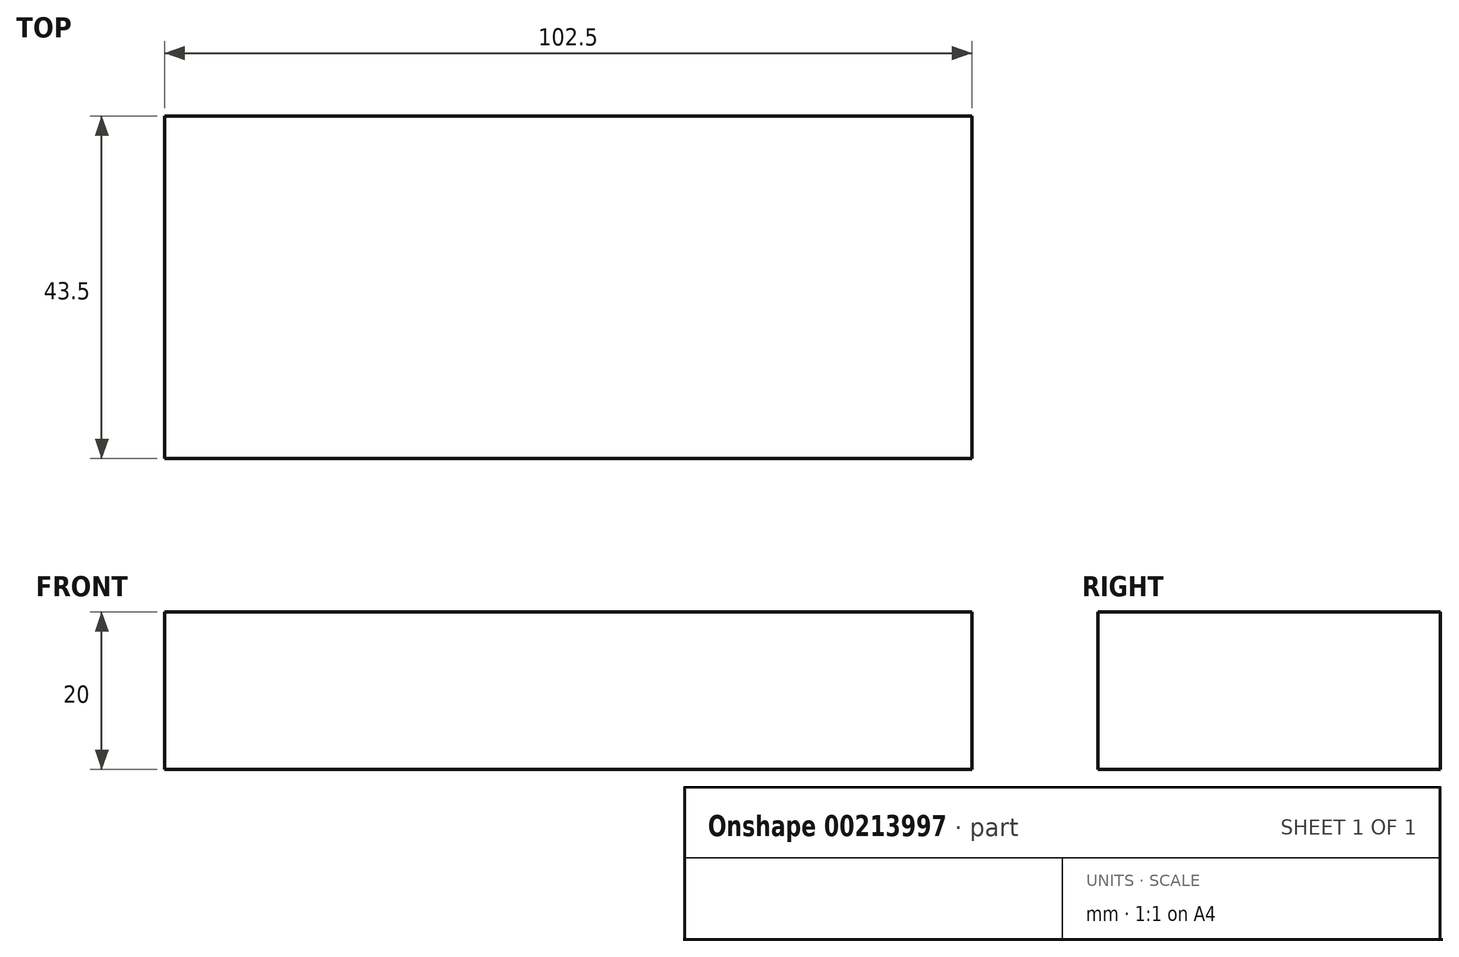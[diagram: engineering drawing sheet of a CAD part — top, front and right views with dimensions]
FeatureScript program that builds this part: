
annotation { "Feature Type Name" : "Feature", "Feature Type Description" : "" }
export const myFeature = defineFeature(function(context is Context, id is Id, definition is map)
    precondition{}
    {
        {
            var Q0;
            Q0=qCreatedBy(makeId("Top.planeOp"),FACE);
            var sketch = newSketch(context, id + "F0", { "sketchPlane" : qUnion([Q0])});
            skLineSegment(sketch, "E0.bottom", {"start": v(-51.25, 21.75) * mm, "end": v(51.25, 21.75) * mm});
            skLineSegment(sketch, "E0.top", {"start": v(-51.25, -21.75) * mm, "end": v(51.25, -21.75) * mm});
            skLineSegment(sketch, "E0.left", {"start": v(-51.25, 21.75) * mm, "end": v(-51.25, -21.75) * mm});
            skLineSegment(sketch, "E0.right", {"start": v(51.25, 21.75) * mm, "end": v(51.25, -21.75) * mm});
            skPoint(sketch, "E0.middle", {"position": v(0, 0) * mm});
            skSolve(sketch);
        }
        {
            var Q0;
            Q0=makeQuery(id+"F0.imprint","IMPRINT",FACE,{"disambiguationData":[TD([[makeQuery(id+"F0.imprint","IMPRINT",EDGE,{"derivedFrom":sQuery(id+"F0.wireOp",EDGE,"E0.bottom")}),-1.0]])]});
            extrude(context, id + "F1", {"entities" : qUnion([Q0]), "depth" : 20 * mm});
        }
    });
